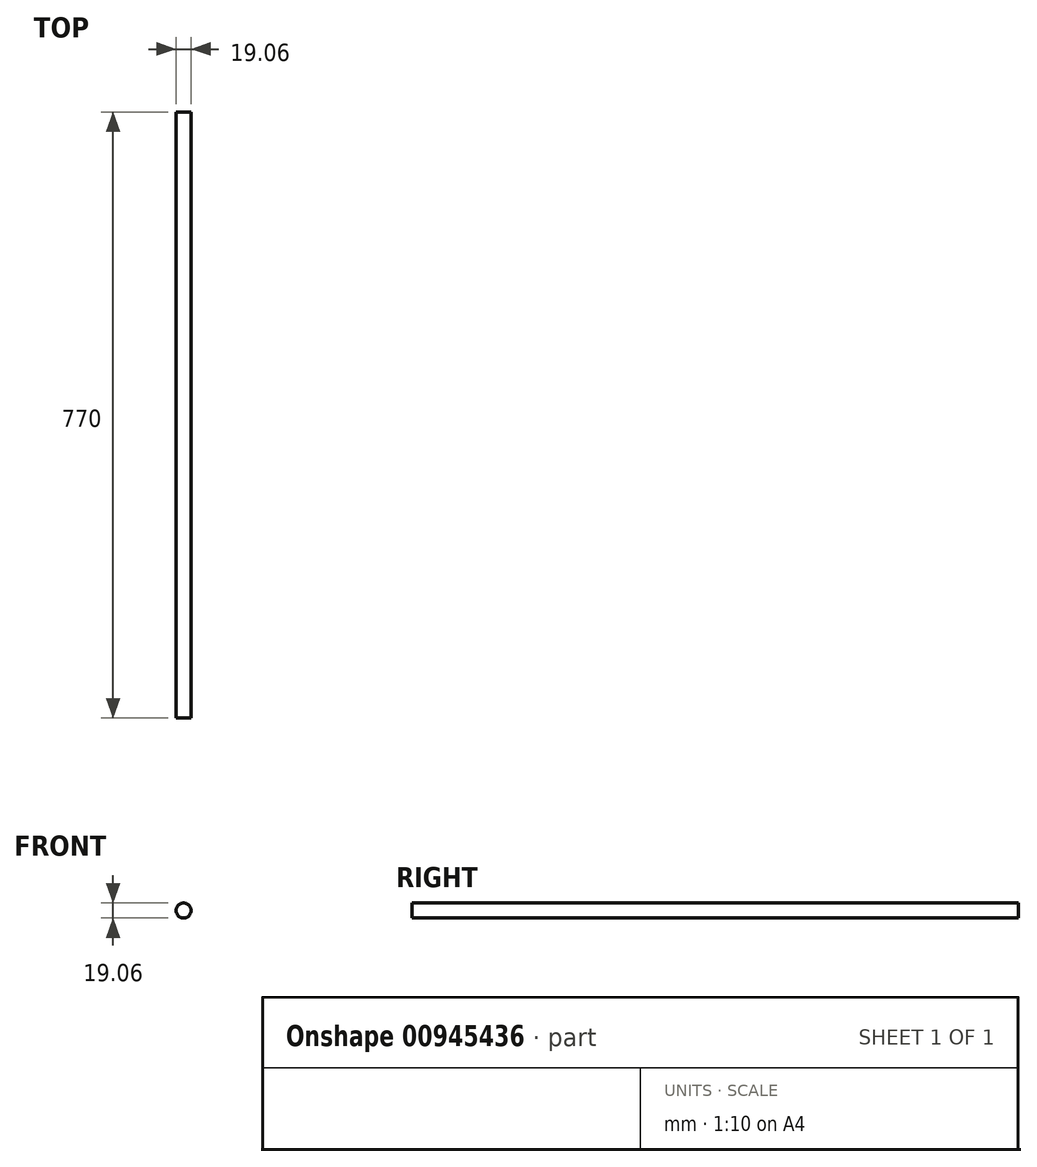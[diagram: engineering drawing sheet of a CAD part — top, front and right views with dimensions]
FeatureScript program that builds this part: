
annotation { "Feature Type Name" : "Feature", "Feature Type Description" : "" }
export const myFeature = defineFeature(function(context is Context, id is Id, definition is map)
    precondition{}
    {
        {
            var Q0;
            Q0=qCreatedBy(makeId("Front.planeOp"),FACE);
            var sketch = newSketch(context, id + "F0", { "sketchPlane" : qUnion([Q0])});
            skCircle(sketch, "E0", {"center": v(0, 0) * mm, "radius": 9.53 * mm});
            skSolve(sketch);
        }
        {
            var Q0;
            Q0=sQuery(id+"F0.wireOp",EDGE,"E0");
            extrude(context, id + "F1", {"bodyType" : ToolBodyType.SURFACE, "surfaceEntities" : qUnion([Q0]), "depth" : 770 * mm, "offsetDistance" : 25.4 * mm});
        }
    });
